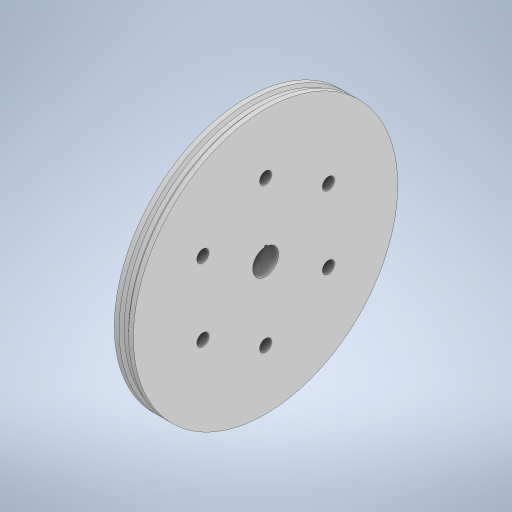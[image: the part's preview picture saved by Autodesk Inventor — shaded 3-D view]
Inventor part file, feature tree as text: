
AUTODESK INVENTOR PART (.ipt)
format: ipt  version: 2024 (Build 280153000, 153)  size: 277,504 bytes
history: native  units: mm
features: sketch x4, thicken_offset x4, revolve x1, extrude x1, emboss x1
ambient origin geometry x8: Origin, YZ Plane, XZ Plane, XY Plane, X Axis, Y Axis, Z Axis, Center Point
bodies: Solid1 (feature_tree)
feature tree (11):
  sketch  "Sketch1"  dims[d0=40.0mm d5=90.0deg]
  sketch  "Sketch2"  dims[d6=10.0mm d7=10.0mm]
  revolve  "Revolution1"  Angle=90.0deg
  thicken_offset  "Thicken1"
  thicken_offset  "Thicken2"
  thicken_offset  "Thicken3"
  thicken_offset  "Thicken4"
  extrude  "Extrusion1"  Depth=10.0mm
  emboss  "Emboss1"
  sketch  "Sketch3"  dims[d8=10.0mm]
  sketch  "Sketch4"  dims[d9=10.0mm d10=10.0mm d11=10.0mm d12=10.0mm d13=10.0mm d15=60.0mm d17=360.0deg d19=60.0mm d20=0.0mm d23=10.0mm d24=10.0mm d25=60.0mm d26=0.0mm]
